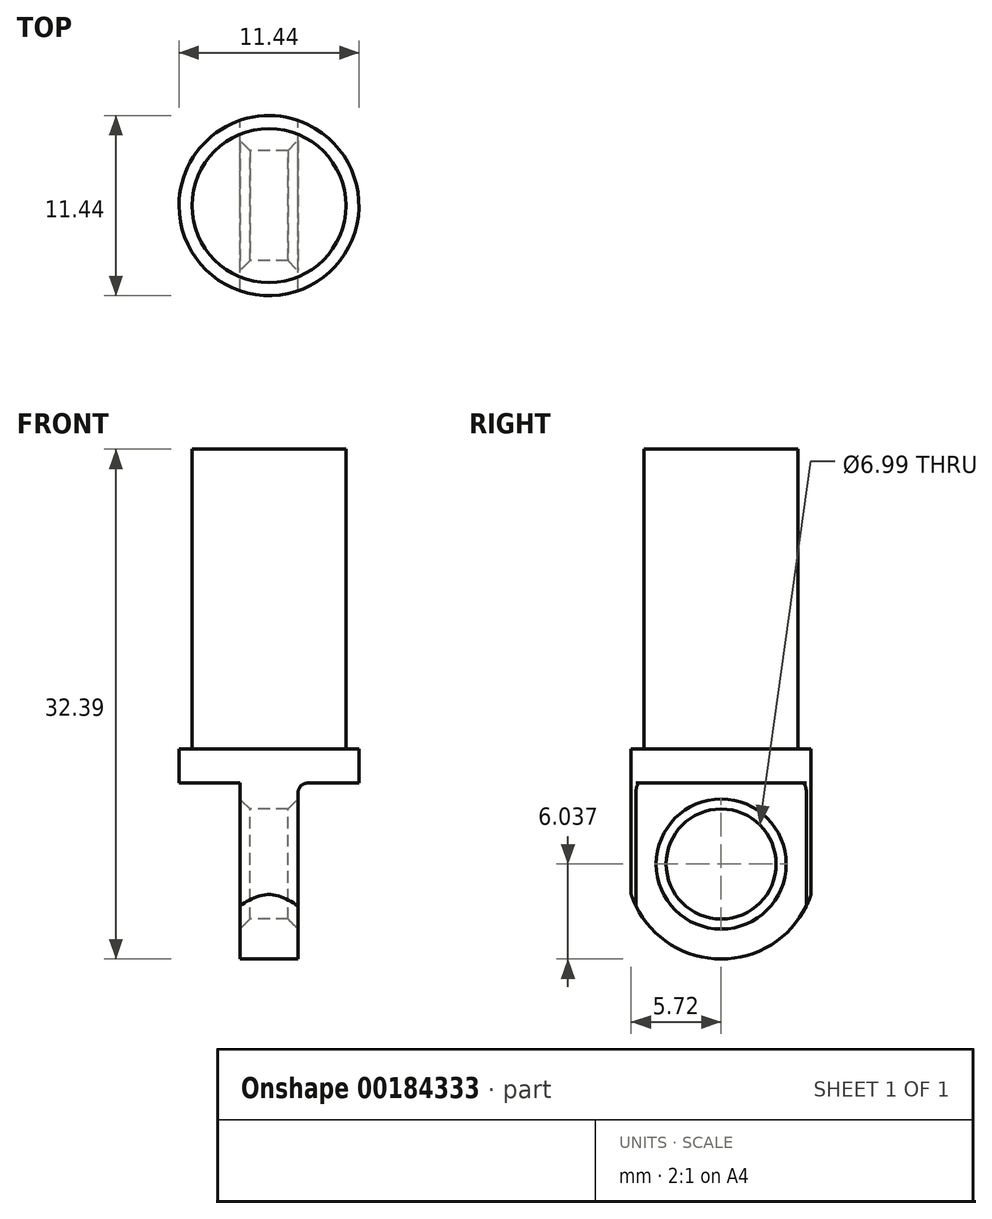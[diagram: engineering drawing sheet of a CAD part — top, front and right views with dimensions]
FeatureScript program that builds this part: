
annotation { "Feature Type Name" : "Feature", "Feature Type Description" : "" }
export const myFeature = defineFeature(function(context is Context, id is Id, definition is map)
    precondition{}
    {
        {
            var Q0;
            Q0=qCreatedBy(makeId("Top.planeOp"),FACE);
            var sketch = newSketch(context, id + "F0", { "sketchPlane" : qUnion([Q0])});
            skCircle(sketch, "E0", {"center": v(0, 0) * mm, "radius": 4.89 * mm});
            skSolve(sketch);
        }
        {
            var Q0;
            Q0 = qSketchRegion(id + "F0", true);
            extrude(context, id + "F1", {"entities" : qUnion([Q0]), "depth" : 19.05 * mm});
        }
        {
            var Q0;
            Q0=makeQuery(id+"F1.opExtrude","CAP_FACE",FACE,{"disambiguationData":[OSD([sQuery(id+"F0.wireOp",EDGE,"E0")])],"isStart":true});
            var sketch = newSketch(context, id + "F2", { "sketchPlane" : qUnion([Q0])});
            skCircle(sketch, "E1", {"center": v(0, 0) * mm, "radius": 5.72 * mm});
            skSolve(sketch);
        }
        {
            var Q0;
            Q0 = qSketchRegion(id + "F2", true);
            extrude(context, id + "F3", {"entities" : qUnion([Q0]), "operationType" : NewBodyOperationType.ADD, "depth" : 2.16 * mm});
        }
        {
            var Q0;
            Q0=qCreatedBy(makeId("Right.planeOp"),FACE);
            var sketch = newSketch(context, id + "F4", { "sketchPlane" : qUnion([Q0])});
            skLineSegment(sketch, "E2", {"start": v(-5.72, -2.16) * mm, "end": v(5.71, -2.16) * mm});
            skLineSegment(sketch, "E3", {"start": v(-5.72, -2.16) * mm, "end": v(-5.72, -9.23) * mm});
            skLineSegment(sketch, "E4", {"start": v(5.72, -9.23) * mm, "end": v(5.71, -2.16) * mm});
            skLineSegment(sketch, "E5", {"start": v(0, 0) * mm, "end": v(0, -13.97) * mm, "construction": true});
            skPoint(sketch, "E6", {"position": v(0, -2.16) * mm});
            skCircle(sketch, "E7", {"center": v(0, -7.3) * mm, "radius": 3.5 * mm});
            skPoint(sketch, "E8", {"position": v(0, -3.81) * mm});
            skArc(sketch, "E9.0", {"start": v(-5.71, -9.23) * mm, "mid": v(0, -13.34) * mm, "end": v(5.72, -9.23) * mm});
            skLineSegment(sketch, "E10", {"start": v(-9.23, -13.97) * mm, "end": v(9.3, -13.97) * mm, "construction": true});
            skSolve(sketch);
        }
        {
            var Q0;
            Q0 = qSketchRegion(id + "F4", true);
            extrude(context, id + "F5", {"entities" : qUnion([Q0]), "operationType" : NewBodyOperationType.ADD, "depth" : 1.84 * mm, "hasSecondDirection" : true, "secondDirectionOppositeDirection" : true, "secondDirectionDepth" : 1.84 * mm});
        }
        {
            var Q0;
            {var subQ0=sQuery(id+"F2.wireOp",EDGE,"E1");var subQ1=sQuery(id+"F4.wireOp",EDGE,"E2");Q0=makeQuery(id+"F5.boolean.opBoolean","SPLIT",FACE,{"disambiguationData":[TD([makeQuery(id+"F5.opExtrude","CAP_FACE",FACE,{"disambiguationData":[OSD([subQ1,sQuery(id+"F4.wireOp",EDGE,"E3"),sQuery(id+"F4.wireOp",EDGE,"E4"),sQuery(id+"F4.wireOp",EDGE,"E7"),sQuery(id+"F4.wireOp",EDGE,"E9.0")])],"isStart":true})])],"derivedFrom":makeQuery(id+"F3.opExtrude","CAP_FACE",FACE,{"disambiguationData":[OSD([subQ0])],"isStart":false})});}
            var sketch = newSketch(context, id + "F6", { "sketchPlane" : qUnion([Q0])});
            skCircle(sketch, "E11", {"center": v(0, 0) * mm, "radius": 5.72 * mm});
            skCircle(sketch, "E12.0", {"center": v(0, 0) * mm, "radius": 8.9 * mm});
            skSolve(sketch);
        }
        {
            var Q0;
            Q0=makeQuery(id+"F6.imprint","IMPRINT",FACE,{"disambiguationData":[TD([[makeQuery(id+"F6.imprint","IMPRINT",EDGE,{"derivedFrom":sQuery(id+"F6.wireOp",EDGE,"E12.0")}),1.0]])]});
            extrude(context, id + "F7", {"entities" : qUnion([Q0]), "operationType" : NewBodyOperationType.REMOVE, "depth" : 25.4 * mm});
        }
        {
            var Q0;
            {var subQ0=sQuery(id+"F4.wireOp",EDGE,"E2");Q0=makeQuery(id+"F5.boolean.opBoolean","SPLIT",EDGE,{"disambiguationData":[topologyDisambiguationEdgeConnected([makeQuery(id+"F3.opExtrude","CAP_FACE",FACE,{"disambiguationData":[OSD([sQuery(id+"F2.wireOp",EDGE,"E1")])],"isStart":false}),makeQuery(id+"F5.opExtrude","CAP_FACE",FACE,{"disambiguationData":[OSD([subQ0,sQuery(id+"F4.wireOp",EDGE,"E3"),sQuery(id+"F4.wireOp",EDGE,"E4"),sQuery(id+"F4.wireOp",EDGE,"E7"),sQuery(id+"F4.wireOp",EDGE,"E9.0")])],"isStart":false})])],"derivedFrom":makeQuery(id+"F5.opExtrude","CAP_EDGE",EDGE,{"disambiguationData":[OSD([subQ0])],"isStart":false})});}
            var Q1;
            {var subQ0=sQuery(id+"F4.wireOp",EDGE,"E2");Q1=makeQuery(id+"F5.boolean.opBoolean","SPLIT",EDGE,{"disambiguationData":[topologyDisambiguationEdgeConnected([makeQuery(id+"F3.opExtrude","CAP_FACE",FACE,{"disambiguationData":[OSD([sQuery(id+"F2.wireOp",EDGE,"E1")])],"isStart":false}),makeQuery(id+"F5.opExtrude","CAP_FACE",FACE,{"disambiguationData":[OSD([subQ0,sQuery(id+"F4.wireOp",EDGE,"E3"),sQuery(id+"F4.wireOp",EDGE,"E4"),sQuery(id+"F4.wireOp",EDGE,"E7"),sQuery(id+"F4.wireOp",EDGE,"E9.0")])],"isStart":true})])],"derivedFrom":makeQuery(id+"F5.opExtrude","CAP_EDGE",EDGE,{"disambiguationData":[OSD([subQ0])],"isStart":true})});}
            fillet(context, id + "F8", {"entities" : qUnion([Q0, Q1]), "radius" : 0.64 * mm, "tangentPropagation" : true, "allowEdgeOverflow" : false});
        }
        {
            var Q0;
            Q0=makeQuery(id+"F5.opExtrude","CAP_EDGE",EDGE,{"disambiguationData":[OSD([sQuery(id+"F4.wireOp",EDGE,"E7")])],"isStart":true});
            var Q1;
            Q1=makeQuery(id+"F5.opExtrude","CAP_EDGE",EDGE,{"disambiguationData":[OSD([sQuery(id+"F4.wireOp",EDGE,"E7")])],"isStart":false});
            chamfer(context, id + "F9", {"entities" : qUnion([Q0, Q1]), "width" : 0.64 * mm, "tangentPropagation" : true});
        }
    });
